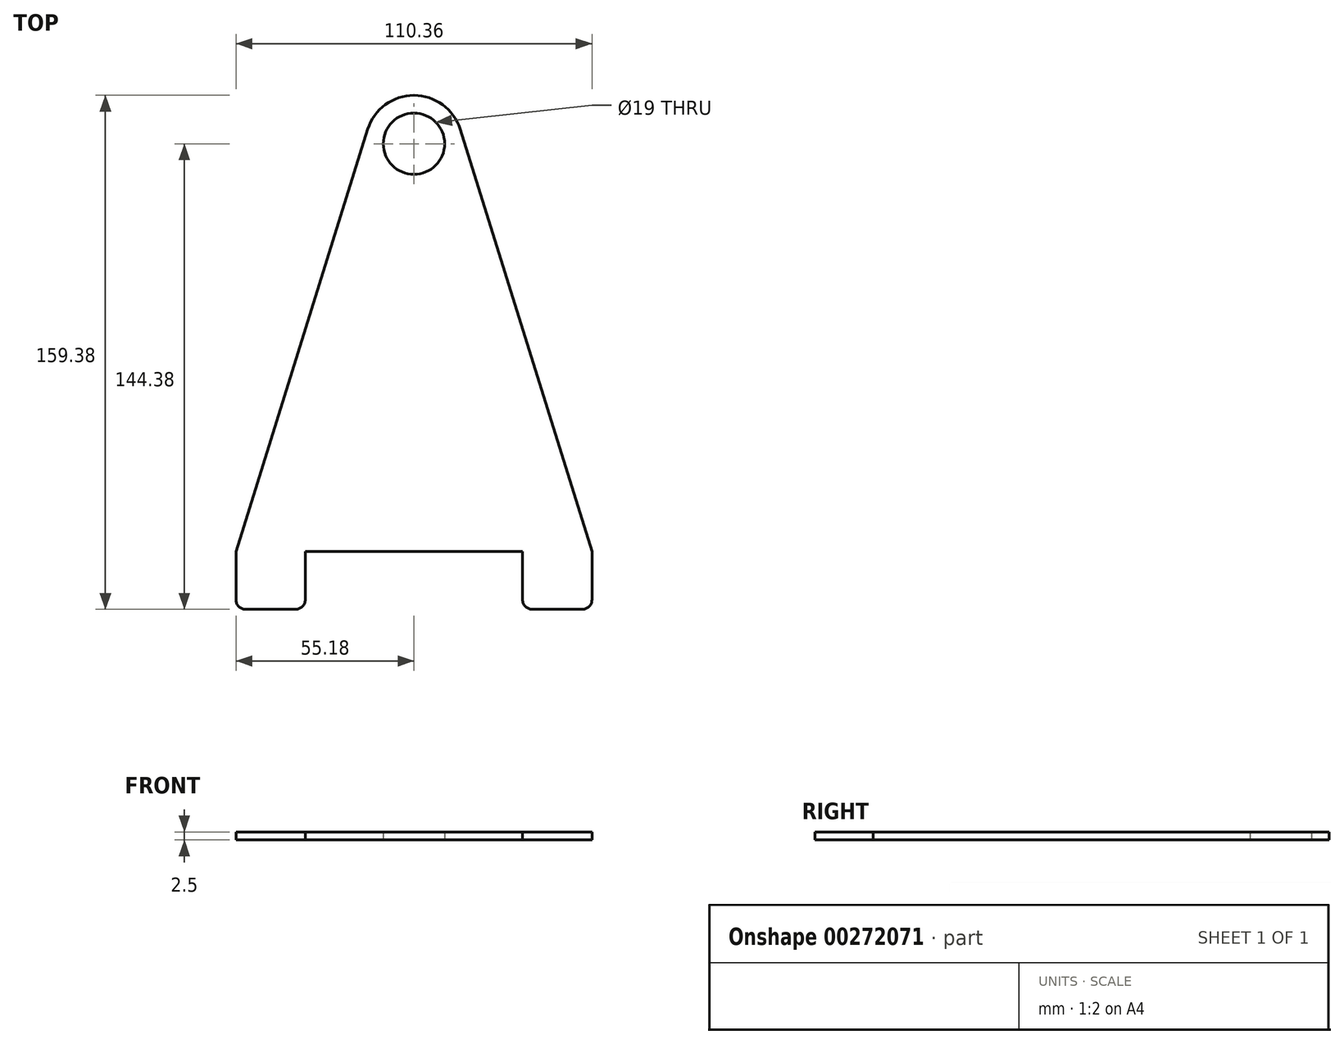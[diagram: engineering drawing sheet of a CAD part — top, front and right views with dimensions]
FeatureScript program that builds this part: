
annotation { "Feature Type Name" : "Feature", "Feature Type Description" : "" }
export const myFeature = defineFeature(function(context is Context, id is Id, definition is map)
    precondition{}
    {
        {
            var Q0;
            Q0=qCreatedBy(makeId("Top.planeOp"),FACE);
            var sketch = newSketch(context, id + "F0", { "sketchPlane" : qUnion([Q0])});
            skCircle(sketch, "E0", {"center": v(0, 61.45) * mm, "radius": 9.5 * mm});
            skCircle(sketch, "E1", {"center": v(0, 61.45) * mm, "radius": 15 * mm});
            skLineSegment(sketch, "E2", {"start": v(-14.32, 65.92) * mm, "end": v(-55.18, -64.93) * mm});
            skLineSegment(sketch, "E3", {"start": v(-55.18, -64.93) * mm, "end": v(-55.18, -79.93) * mm});
            skLineSegment(sketch, "E4", {"start": v(-33.68, -79.93) * mm, "end": v(-33.68, -64.93) * mm});
            skLineSegment(sketch, "E5.MirrorCS", {"start": v(14.32, 65.92) * mm, "end": v(55.18, -64.93) * mm});
            skLineSegment(sketch, "E6.MirrorCS", {"start": v(55.18, -64.93) * mm, "end": v(55.18, -79.93) * mm});
            skLineSegment(sketch, "E7.MirrorCS", {"start": v(33.68, -79.93) * mm, "end": v(33.68, -64.93) * mm});
            skLineSegment(sketch, "E8", {"start": v(-33.68, -64.93) * mm, "end": v(33.68, -64.93) * mm});
            skLineSegment(sketch, "E9", {"start": v(-52.18, -82.93) * mm, "end": v(-36.68, -82.93) * mm});
            skLineSegment(sketch, "E10", {"start": v(36.68, -82.93) * mm, "end": v(52.18, -82.93) * mm});
            skPoint(sketch, "E11.visualSharp", {"position": v(-55.18, -82.93) * mm});
            skArc(sketch, "E11.filletArc", {"start": v(-55.18, -79.93) * mm, "mid": v(-54.3, -82.05) * mm, "end": v(-52.18, -82.93) * mm});
            skPoint(sketch, "E12.visualSharp", {"position": v(-33.68, -82.93) * mm});
            skArc(sketch, "E12.filletArc", {"start": v(-36.68, -82.93) * mm, "mid": v(-34.56, -82.05) * mm, "end": v(-33.68, -79.93) * mm});
            skPoint(sketch, "E13.visualSharp", {"position": v(33.68, -82.93) * mm});
            skArc(sketch, "E13.filletArc", {"start": v(33.68, -79.93) * mm, "mid": v(34.56, -82.05) * mm, "end": v(36.68, -82.93) * mm});
            skPoint(sketch, "E14.visualSharp", {"position": v(55.18, -82.93) * mm});
            skArc(sketch, "E14.filletArc", {"start": v(52.18, -82.93) * mm, "mid": v(54.3, -82.05) * mm, "end": v(55.18, -79.93) * mm});
            skPoint(sketch, "E15", {"position": v(0, -64.93) * mm});
            skSolve(sketch);
        }
        {
            var Q0;
            Q0=makeQuery(id+"F0.imprint","IMPRINT",FACE,{"disambiguationData":[TD([[makeQuery(id+"F0.imprint","IMPRINT",EDGE,{"derivedFrom":sQuery(id+"F0.wireOp",EDGE,"E0")}),-1.0]])]});
            var Q1;
            {var subQ1=sQuery(id+"F0.wireOp",EDGE,"E2");Q1=makeQuery(id+"F0.imprint","IMPRINT",FACE,{"disambiguationData":[TD([[makeQuery(id+"F0.imprint","IMPRINT",EDGE,{"derivedFrom":subQ1}),1.0]])]});}
            extrude(context, id + "F1", {"entities" : qUnion([Q0, Q1]), "depth" : 2.5 * mm});
        }
    });
